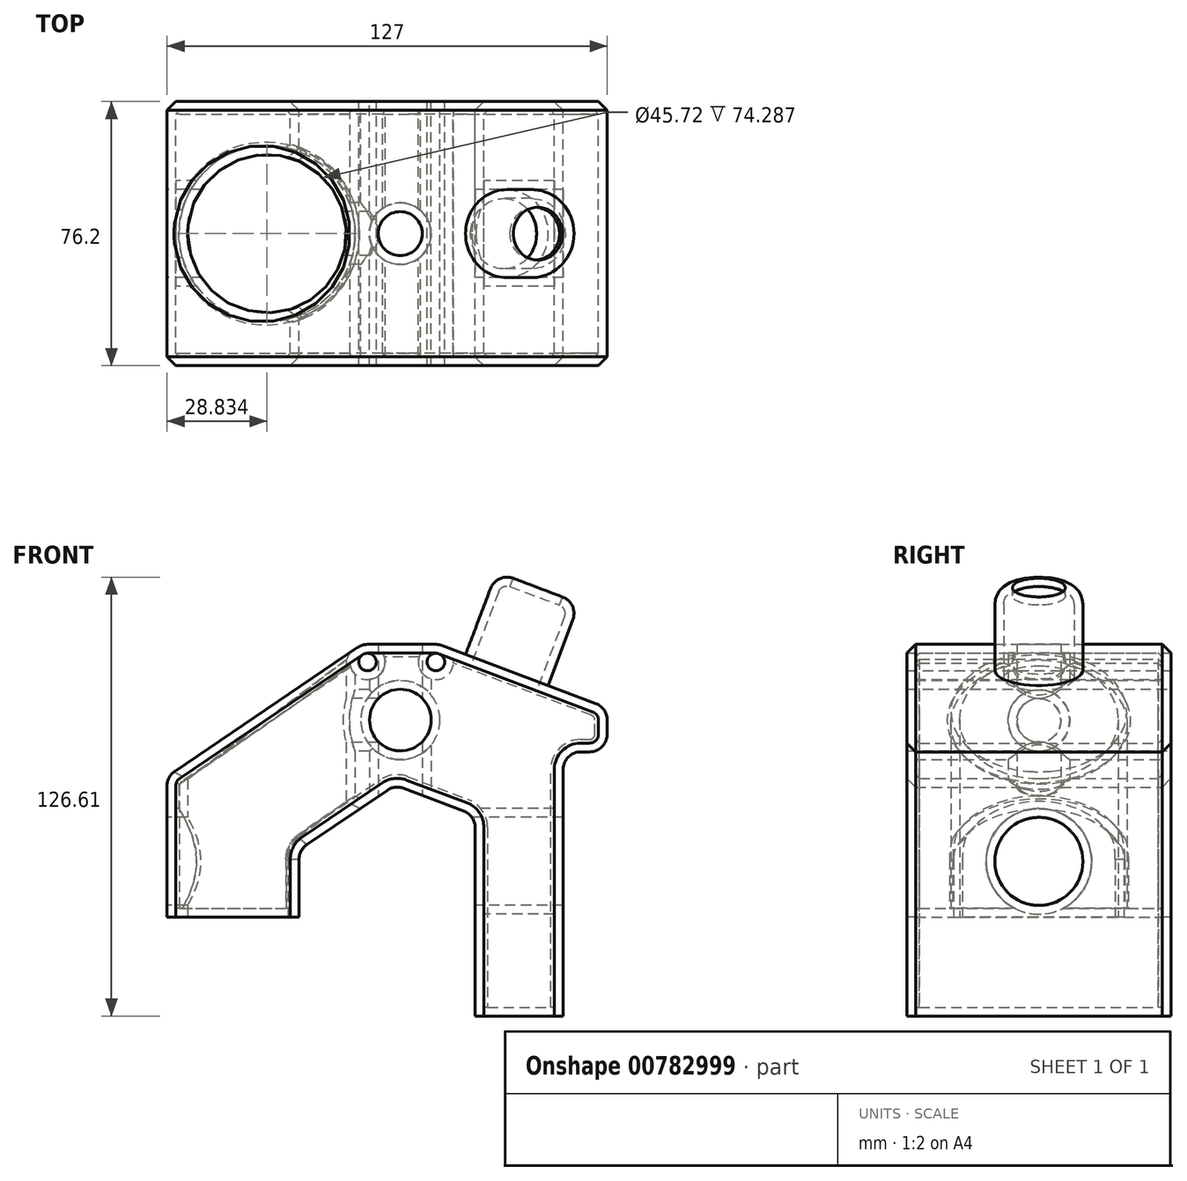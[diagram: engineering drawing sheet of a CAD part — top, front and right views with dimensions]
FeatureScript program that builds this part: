
annotation { "Feature Type Name" : "Feature", "Feature Type Description" : "" }
export const myFeature = defineFeature(function(context is Context, id is Id, definition is map)
    precondition{}
    {
        {
            var Q0;
            Q0=qCreatedBy(makeId("Front.planeOp"),FACE);
            var sketch = newSketch(context, id + "F0", { "sketchPlane" : qUnion([Q0])});
            skLineSegment(sketch, "E0", {"start": v(19.56, 49.31) * mm, "end": v(-0.17, 49.31) * mm});
            skLineSegment(sketch, "E1", {"start": v(-3.02, 48.44) * mm, "end": v(-55.78, 12.72) * mm});
            skLineSegment(sketch, "E2", {"start": v(-58.01, 8.52) * mm, "end": v(-58.01, -29.43) * mm});
            skLineSegment(sketch, "E3", {"start": v(-58.01, -29.43) * mm, "end": v(-19.91, -29.43) * mm});
            skLineSegment(sketch, "E4", {"start": v(-19.91, -29.43) * mm, "end": v(-19.91, -12.67) * mm});
            skLineSegment(sketch, "E5", {"start": v(-17.68, -8.46) * mm, "end": v(5.55, 7.26) * mm});
            skLineSegment(sketch, "E6", {"start": v(10.19, 7.81) * mm, "end": v(27.6, 1.24) * mm});
            skLineSegment(sketch, "E7", {"start": v(30.89, -3.51) * mm, "end": v(30.89, -57.89) * mm});
            skLineSegment(sketch, "E8", {"start": v(30.89, -57.89) * mm, "end": v(56.29, -57.89) * mm});
            skLineSegment(sketch, "E9", {"start": v(56.29, -57.89) * mm, "end": v(56.29, 13.23) * mm});
            skLineSegment(sketch, "E10", {"start": v(61.37, 18.31) * mm, "end": v(63.9, 18.31) * mm});
            skLineSegment(sketch, "E11", {"start": v(68.99, 23.4) * mm, "end": v(68.99, 27.5) * mm});
            skLineSegment(sketch, "E12", {"start": v(65.7, 32.25) * mm, "end": v(21.35, 48.99) * mm});
            skPoint(sketch, "E13.visualSharp", {"position": v(-58.01, 11.21) * mm});
            skArc(sketch, "E13.filletArc", {"start": v(-55.78, 12.72) * mm, "mid": v(-57.42, 10.9) * mm, "end": v(-58.01, 8.52) * mm});
            skPoint(sketch, "E14.visualSharp", {"position": v(56.29, 18.31) * mm});
            skArc(sketch, "E14.filletArc", {"start": v(61.37, 18.31) * mm, "mid": v(57.77, 16.82) * mm, "end": v(56.29, 13.23) * mm});
            skPoint(sketch, "E15.visualSharp", {"position": v(-1.73, 49.31) * mm});
            skArc(sketch, "E15.filletArc", {"start": v(-0.17, 49.31) * mm, "mid": v(-1.66, 49.1) * mm, "end": v(-3.02, 48.44) * mm});
            skPoint(sketch, "E16.visualSharp", {"position": v(20.48, 49.31) * mm});
            skArc(sketch, "E16.filletArc", {"start": v(21.35, 48.99) * mm, "mid": v(20.47, 49.23) * mm, "end": v(19.56, 49.31) * mm});
            skPoint(sketch, "E17.visualSharp", {"position": v(68.99, 18.31) * mm});
            skArc(sketch, "E17.filletArc", {"start": v(63.9, 18.31) * mm, "mid": v(67.5, 19.8) * mm, "end": v(68.99, 23.4) * mm});
            skPoint(sketch, "E18.visualSharp", {"position": v(68.99, 31.01) * mm});
            skArc(sketch, "E18.filletArc", {"start": v(68.99, 27.5) * mm, "mid": v(68.08, 30.39) * mm, "end": v(65.7, 32.25) * mm});
            skPoint(sketch, "E19.visualSharp", {"position": v(7.73, 8.74) * mm});
            skArc(sketch, "E19.filletArc", {"start": v(10.19, 7.81) * mm, "mid": v(7.8, 8.1) * mm, "end": v(5.55, 7.26) * mm});
            skPoint(sketch, "E20.visualSharp", {"position": v(-19.91, -9.97) * mm});
            skArc(sketch, "E20.filletArc", {"start": v(-17.68, -8.46) * mm, "mid": v(-19.32, -10.29) * mm, "end": v(-19.91, -12.67) * mm});
            skPoint(sketch, "E21.visualSharp", {"position": v(30.89, 0) * mm});
            skArc(sketch, "E21.filletArc", {"start": v(30.89, -3.51) * mm, "mid": v(29.98, -0.62) * mm, "end": v(27.6, 1.24) * mm});
            skPoint(sketch, "E22", {"position": v(9.31, 27.5) * mm});
            skCircle(sketch, "E23", {"center": v(-0.17, 44.23) * mm, "radius": 2.54 * mm});
            skCircle(sketch, "E24", {"center": v(19.56, 44.23) * mm, "radius": 2.54 * mm});
            skCircle(sketch, "E25", {"center": v(9.31, 27.5) * mm, "radius": 8.9 * mm});
            skSolve(sketch);
        }
        {
            var Q0;
            Q0=makeQuery(id+"F0.imprint","IMPRINT",FACE,{"disambiguationData":[TD([[makeQuery(id+"F0.imprint","IMPRINT",EDGE,{"derivedFrom":sQuery(id+"F0.wireOp",EDGE,"E0")}),1.0]])]});
            extrude(context, id + "F1", {"entities" : qUnion([Q0]), "endBound" : BoundingType.SYMMETRIC, "depth" : 76.2 * mm, "offsetDistance" : 25.4 * mm});
        }
        {
            var Q0;
            Q0=makeQuery(id+"F1.opExtrude","CAP_EDGE",EDGE,{"disambiguationData":[OSD([sQuery(id+"F0.wireOp",EDGE,"E2")])],"isStart":false});
            var Q1;
            Q1=makeQuery(id+"F1.opExtrude","CAP_EDGE",EDGE,{"disambiguationData":[OSD([sQuery(id+"F0.wireOp",EDGE,"E13.filletArc")])],"isStart":false});
            var Q2;
            Q2=makeQuery(id+"F1.opExtrude","CAP_EDGE",EDGE,{"disambiguationData":[OSD([sQuery(id+"F0.wireOp",EDGE,"E7")])],"isStart":false});
            var Q3;
            Q3=makeQuery(id+"F1.opExtrude","CAP_EDGE",EDGE,{"disambiguationData":[OSD([sQuery(id+"F0.wireOp",EDGE,"E2")])],"isStart":true});
            var Q4;
            Q4=makeQuery(id+"F1.opExtrude","CAP_EDGE",EDGE,{"disambiguationData":[OSD([sQuery(id+"F0.wireOp",EDGE,"E13.filletArc")])],"isStart":true});
            var Q5;
            Q5=makeQuery(id+"F1.opExtrude","CAP_EDGE",EDGE,{"disambiguationData":[OSD([sQuery(id+"F0.wireOp",EDGE,"E7")])],"isStart":true});
            chamfer(context, id + "F2", {"entities" : qUnion([Q0, Q1, Q2, Q3, Q4, Q5]), "width" : 2.54 * mm, "tangentPropagation" : true});
        }
        {
            var Q0;
            Q0=qCreatedBy(makeId("Top.planeOp"),FACE);
            var sketch = newSketch(context, id + "F3", { "sketchPlane" : qUnion([Q0])});
            skCircle(sketch, "E26", {"center": v(-29.18, 0) * mm, "radius": 22.86 * mm});
            skSolve(sketch);
        }
        {
            var Q0;
            Q0 = qSketchRegion(id + "F3", true);
            extrude(context, id + "F4", {"entities" : qUnion([Q0]), "operationType" : NewBodyOperationType.REMOVE, "endBound" : BoundingType.SYMMETRIC, "depth" : 101.6 * mm, "offsetDistance" : 25.4 * mm});
        }
        {
            var Q0;
            Q0=makeQuery(id+"F4.boolean.opBoolean","INTERSECT",EDGE,{"disambiguationData":[OD(0.0)],"derivedFrom":[makeQuery(id+"F1.opExtrude","SWEPT_FACE",FACE,{"disambiguationData":[OSD([sQuery(id+"F0.wireOp",EDGE,"E4")])]}),makeQuery(id+"F4.opExtrude","SWEPT_FACE",FACE,{"disambiguationData":[OSD([sQuery(id+"F3.wireOp",EDGE,"E26")])]})]});
            var Q1;
            Q1=makeQuery(id+"F4.boolean.opBoolean","INTERSECT",EDGE,{"disambiguationData":[OD(0.0)],"derivedFrom":[makeQuery(id+"F1.opExtrude","SWEPT_FACE",FACE,{"disambiguationData":[OSD([sQuery(id+"F0.wireOp",EDGE,"E20.filletArc")])]}),makeQuery(id+"F4.opExtrude","SWEPT_FACE",FACE,{"disambiguationData":[OSD([sQuery(id+"F3.wireOp",EDGE,"E26")])]})]});
            var Q2;
            Q2=makeQuery(id+"F4.boolean.opBoolean","INTERSECT",EDGE,{"derivedFrom":[makeQuery(id+"F1.opExtrude","SWEPT_FACE",FACE,{"disambiguationData":[OSD([sQuery(id+"F0.wireOp",EDGE,"E1")])]}),makeQuery(id+"F4.opExtrude","SWEPT_FACE",FACE,{"disambiguationData":[OSD([sQuery(id+"F3.wireOp",EDGE,"E26")])]})]});
            chamfer(context, id + "F5", {"entities" : qUnion([Q0, Q1, Q2]), "width" : 2.54 * mm, "tangentPropagation" : true});
        }
        {
            var Q0;
            Q0=qCreatedBy(makeId("Right.planeOp"),FACE);
            var sketch = newSketch(context, id + "F6", { "sketchPlane" : qUnion([Q0])});
            skCircle(sketch, "E27", {"center": v(0, -13.29) * mm, "radius": 12.7 * mm});
            skSolve(sketch);
        }
        {
            var Q0;
            Q0 = qSketchRegion(id + "F6", true);
            var Q1;
            Q1 = qConstructionFilter(qBodyType(qCreatedBy(id + "F6" ,EDGE), BodyType.WIRE), ConstructionObject.NO);
            extrude(context, id + "F7", {"entities" : qUnion([Q0]), "operationType" : NewBodyOperationType.REMOVE, "surfaceEntities" : qUnion([Q1]), "endBound" : BoundingType.SYMMETRIC, "depth" : 228.6 * mm, "offsetDistance" : 25.4 * mm});
        }
        {
            var Q0;
            Q0=qCreatedBy(makeId("Right.planeOp"),FACE);
            var sketch = newSketch(context, id + "F8", { "sketchPlane" : qUnion([Q0])});
            skCircle(sketch, "E28", {"center": v(0, 27.35) * mm, "radius": 6.35 * mm});
            skSolve(sketch);
        }
        {
            var Q0;
            Q0 = qSketchRegion(id + "F8", true);
            extrude(context, id + "F9", {"entities" : qUnion([Q0]), "operationType" : NewBodyOperationType.REMOVE, "depth" : 12.7 * mm, "offsetDistance" : 25.4 * mm, "hasSecondDirection" : true, "secondDirectionOppositeDirection" : true, "secondDirectionDepth" : 50.8 * mm});
        }
        {
            var Q0;
            Q0=qCreatedBy(makeId("Top.planeOp"),FACE);
            var sketch = newSketch(context, id + "F10", { "sketchPlane" : qUnion([Q0])});
            skCircle(sketch, "E29", {"center": v(9.27, 0) * mm, "radius": 6.35 * mm});
            skSolve(sketch);
        }
        {
            var Q0;
            Q0 = qSketchRegion(id + "F10", true);
            extrude(context, id + "F11", {"entities" : qUnion([Q0]), "operationType" : NewBodyOperationType.REMOVE, "endBound" : BoundingType.THROUGH_ALL, "depth" : 86.36 * mm, "offsetDistance" : 25.4 * mm});
        }
        {
            var Q0;
            Q0=makeQuery(id+"F1.opExtrude","SWEPT_FACE",FACE,{"disambiguationData":[OSD([sQuery(id+"F0.wireOp",EDGE,"E12")])]});
            var sketch = newSketch(context, id + "F12", { "sketchPlane" : qUnion([Q0])});
            skCircle(sketch, "E30", {"center": v(22.63, 0) * mm, "radius": 12.7 * mm});
            skSolve(sketch);
        }
        {
            var Q0;
            Q0 = qSketchRegion(id + "F12", true);
            var Q1;
            Q1=sQuery(id+"F12.wireOp",EDGE,"E30");
            extrude(context, id + "F13", {"entities" : qUnion([Q0]), "operationType" : NewBodyOperationType.ADD, "surfaceEntities" : qUnion([Q1]), "depth" : 25.4 * mm, "offsetDistance" : 25.4 * mm});
        }
        {
            var Q0;
            Q0=makeQuery(id+"F13.opExtrude","CAP_EDGE",EDGE,{"disambiguationData":[OSD([sQuery(id+"F12.wireOp",EDGE,"E30")])],"isStart":false});
            var Q1;
            Q1=makeQuery(id+"F13.opExtrude","CAP_EDGE",EDGE,{"disambiguationData":[OSD([sQuery(id+"F12.wireOp",EDGE,"E30")])],"isStart":true});
            fillet(context, id + "F14", {"entities" : qUnion([Q0, Q1]), "radius" : 5.08 * mm, "tangentPropagation" : true, "allowEdgeOverflow" : false});
        }
        {
            var Q0;
            Q0=makeQuery(id+"F13.opExtrude","CAP_FACE",FACE,{"disambiguationData":[OSD([sQuery(id+"F12.wireOp",EDGE,"E30")])],"isStart":false});
            shell(context, id + "F15", {"entities" : qUnion([Q0]), "thickness" : 2.54 * mm});
        }
    });
